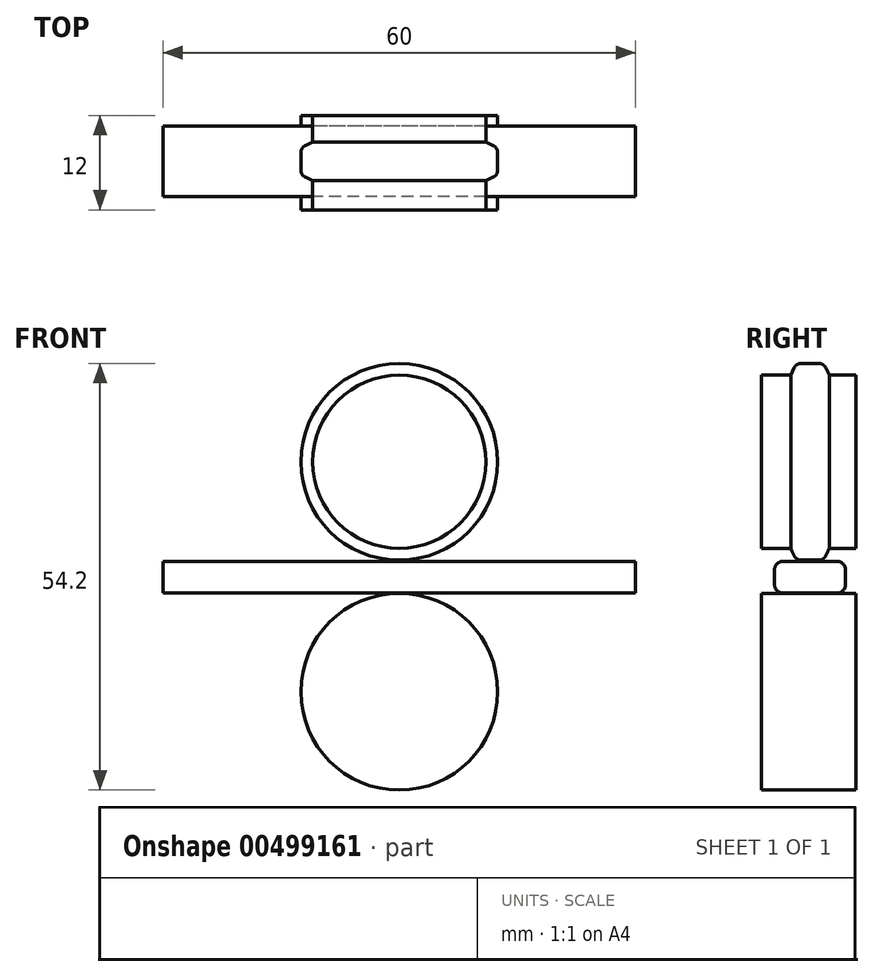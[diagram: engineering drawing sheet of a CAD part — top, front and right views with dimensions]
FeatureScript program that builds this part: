
annotation { "Feature Type Name" : "Feature", "Feature Type Description" : "" }
export const myFeature = defineFeature(function(context is Context, id is Id, definition is map)
    precondition{}
    {
        {
            var Q0;
            Q0=qCreatedBy(makeId("Front.planeOp"),FACE);
            var sketch = newSketch(context, id + "F0", { "sketchPlane" : qUnion([Q0])});
            skCircle(sketch, "E0", {"center": v(0, -14.61) * mm, "radius": 12.5 * mm});
            skSolve(sketch);
        }
        {
            var Q0;
            Q0=qCreatedBy(makeId("Right.planeOp"),FACE);
            var sketch = newSketch(context, id + "F1", { "sketchPlane" : qUnion([Q0])});
            skLineSegment(sketch, "E1.bottom", {"start": v(-9.32, 1.93) * mm, "end": v(-2.32, 1.93) * mm});
            skLineSegment(sketch, "E1.top", {"start": v(-9.32, -2.07) * mm, "end": v(-2.32, -2.07) * mm});
            skLineSegment(sketch, "E1.left", {"start": v(-10.32, 0.93) * mm, "end": v(-10.32, -1.07) * mm});
            skLineSegment(sketch, "E1.right", {"start": v(-1.32, 0.93) * mm, "end": v(-1.32, -1.07) * mm});
            skPoint(sketch, "E2.visualSharp", {"position": v(-10.32, 1.93) * mm});
            skArc(sketch, "E2.filletArc", {"start": v(-9.32, 1.93) * mm, "mid": v(-10.03, 1.64) * mm, "end": v(-10.32, 0.93) * mm});
            skPoint(sketch, "E3.visualSharp", {"position": v(-10.32, -2.07) * mm});
            skArc(sketch, "E3.filletArc", {"start": v(-10.32, -1.07) * mm, "mid": v(-10.03, -1.77) * mm, "end": v(-9.32, -2.07) * mm});
            skPoint(sketch, "E4.visualSharp", {"position": v(-1.32, 1.93) * mm});
            skArc(sketch, "E4.filletArc", {"start": v(-1.32, 0.93) * mm, "mid": v(-1.61, 1.64) * mm, "end": v(-2.32, 1.93) * mm});
            skPoint(sketch, "E5.visualSharp", {"position": v(-1.32, -2.07) * mm});
            skArc(sketch, "E5.filletArc", {"start": v(-2.32, -2.07) * mm, "mid": v(-1.61, -1.77) * mm, "end": v(-1.32, -1.07) * mm});
            skSolve(sketch);
        }
        {
            var Q0;
            Q0 = qSketchRegion(id + "F1", true);
            extrude(context, id + "F2", {"entities" : qUnion([Q0]), "endBound" : BoundingType.SYMMETRIC, "depth" : 60 * mm});
        }
        {
            var Q0;
            Q0=makeQuery(id+"F0.imprint","IMPRINT",FACE,{"disambiguationData":[TD([[makeQuery(id+"F0.imprint","IMPRINT",EDGE,{"derivedFrom":sQuery(id+"F0.wireOp",EDGE,"E0")}),1.0]])]});
            extrude(context, id + "F3", {"entities" : qUnion([Q0]), "depth" : 12 * mm});
        }
        {
            var Q0;
            Q0=qCreatedBy(makeId("Right.planeOp"),FACE);
            var sketch = newSketch(context, id + "F4", { "sketchPlane" : qUnion([Q0])});
            skLineSegment(sketch, "E6", {"start": v(0, 14.6) * mm, "end": v(0, 3.6) * mm});
            skLineSegment(sketch, "E7", {"start": v(0, 3.6) * mm, "end": v(-3.38, 3.6) * mm});
            skLineSegment(sketch, "E8", {"start": v(-3.38, 3.6) * mm, "end": v(-4.08, 2.1) * mm});
            skLineSegment(sketch, "E9", {"start": v(-4.08, 2.1) * mm, "end": v(-7.58, 2.1) * mm});
            skLineSegment(sketch, "E10", {"start": v(-7.58, 2.1) * mm, "end": v(-8.28, 3.6) * mm});
            skLineSegment(sketch, "E11", {"start": v(-8.28, 3.6) * mm, "end": v(-12, 3.6) * mm});
            skLineSegment(sketch, "E12", {"start": v(-12, 3.6) * mm, "end": v(-12, 14.6) * mm});
            skLineSegment(sketch, "E13", {"start": v(-12, 14.6) * mm, "end": v(0, 14.6) * mm});
            skSolve(sketch);
        }
        {
            var Q0;
            Q0=makeQuery(id+"F4.imprint","IMPRINT",FACE,{"disambiguationData":[TD([[makeQuery(id+"F4.imprint","IMPRINT",EDGE,{"derivedFrom":sQuery(id+"F4.wireOp",EDGE,"E6")}),-1.0]])]});
            var Q1;
            Q1=sQuery(id+"F4.wireOp",EDGE,"E13");
            revolve(context, id + "F5", {"entities" : qUnion([Q0]), "axis" : qUnion([Q1]), "revolveType" : RevolveType.FULL});
        }
        {
            var Q0;
            Q0=makeQuery(id+"F5.opRevolve","SWEPT_EDGE",EDGE,{"disambiguationData":[OSD([sQuery(id+"F4.wireOp",EDGE,"E9"),sQuery(id+"F4.wireOp",EDGE,"E10")])]});
            fillet(context, id + "F6", {"entities" : qUnion([Q0]), "radius" : 1 * mm, "tangentPropagation" : true, "allowEdgeOverflow" : false});
        }
        {
            var Q0;
            Q0=makeQuery(id+"F5.opRevolve","SWEPT_EDGE",EDGE,{"disambiguationData":[OSD([sQuery(id+"F4.wireOp",EDGE,"E8"),sQuery(id+"F4.wireOp",EDGE,"E9")])]});
            fillet(context, id + "F7", {"entities" : qUnion([Q0]), "radius" : 1 * mm, "tangentPropagation" : true, "allowEdgeOverflow" : false});
        }
    });
